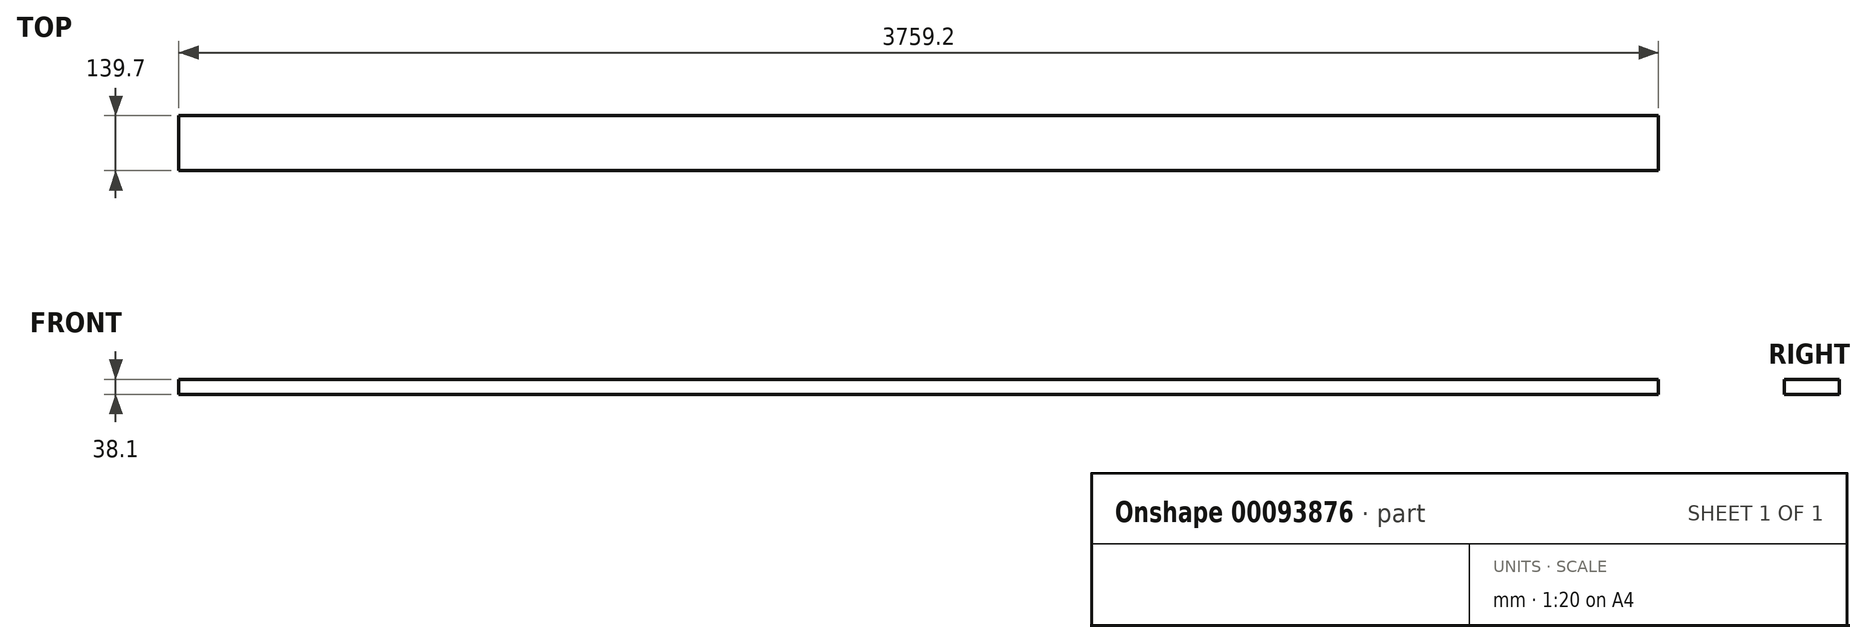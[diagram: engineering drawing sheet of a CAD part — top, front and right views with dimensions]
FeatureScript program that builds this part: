
annotation { "Feature Type Name" : "Feature", "Feature Type Description" : "" }
export const myFeature = defineFeature(function(context is Context, id is Id, definition is map)
    precondition{}
    {
        {
            var Q0;
            Q0=qCreatedBy(makeId("Top.planeOp"),FACE);
            var sketch = newSketch(context, id + "F0", { "sketchPlane" : qUnion([Q0])});
            skLineSegment(sketch, "E0.bottom", {"start": v(-1879.6, 139.7) * mm, "end": v(1879.6, 139.7) * mm});
            skLineSegment(sketch, "E0.top", {"start": v(-1879.6, 0) * mm, "end": v(1879.6, 0) * mm});
            skLineSegment(sketch, "E0.left", {"start": v(-1879.6, 139.7) * mm, "end": v(-1879.6, 0) * mm});
            skLineSegment(sketch, "E0.right", {"start": v(1879.6, 139.7) * mm, "end": v(1879.6, 0) * mm});
            skSolve(sketch);
        }
        {
            var Q0;
            Q0 = qSketchRegion(id + "F0", true);
            extrude(context, id + "F1", {"entities" : qUnion([Q0]), "depth" : 38.1 * mm});
        }
    });
